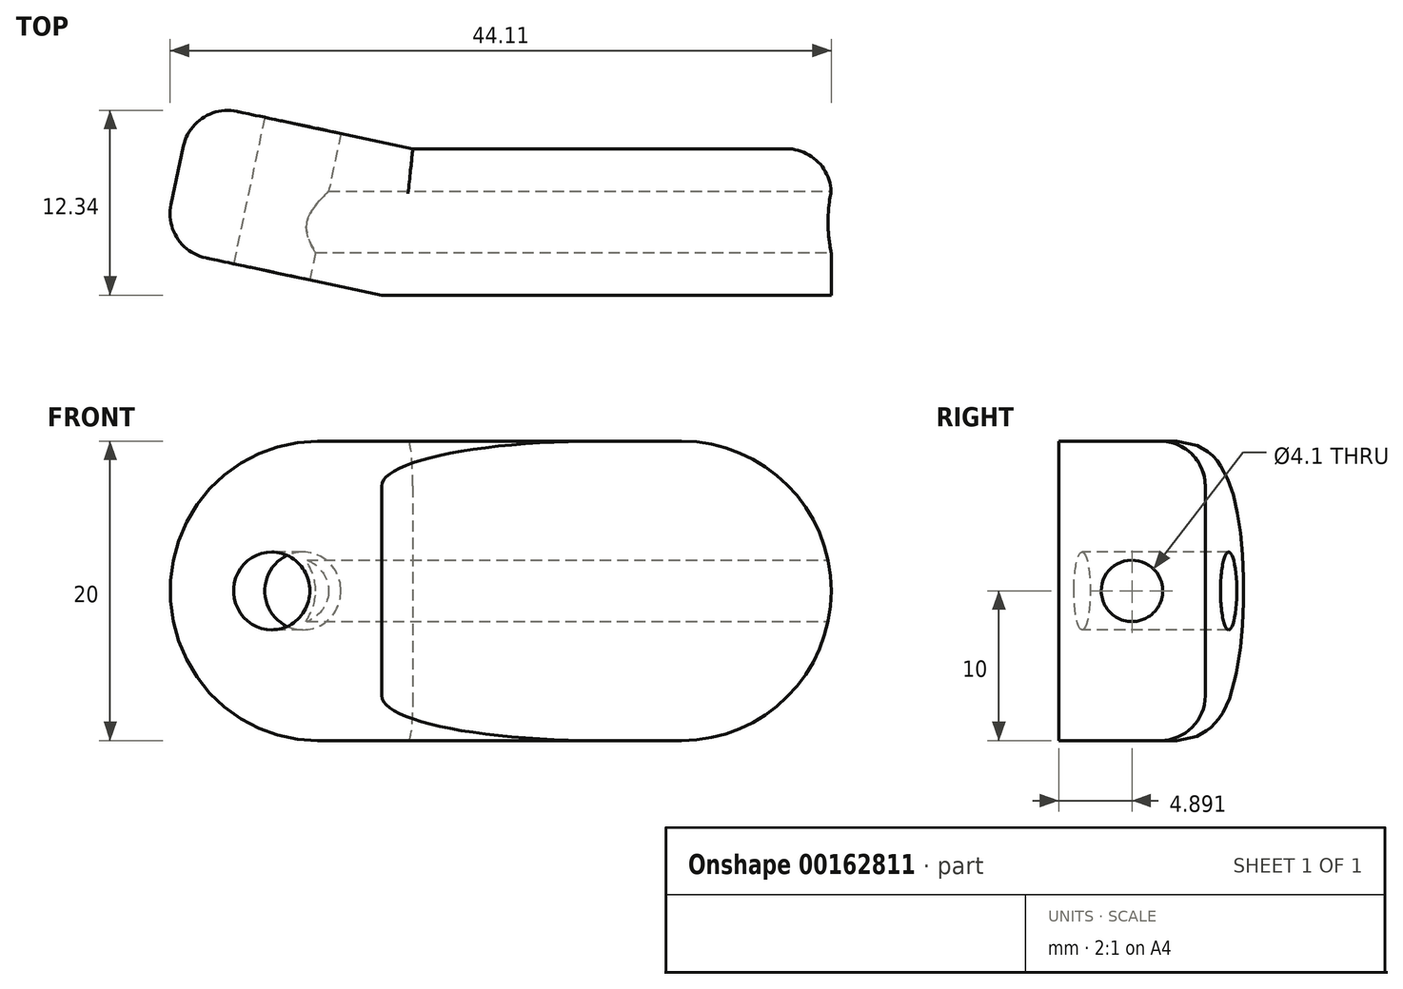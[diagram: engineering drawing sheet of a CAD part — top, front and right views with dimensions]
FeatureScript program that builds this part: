
annotation { "Feature Type Name" : "Feature", "Feature Type Description" : "" }
export const myFeature = defineFeature(function(context is Context, id is Id, definition is map)
    precondition{}
    {
        {
            var Q0;
            Q0=qCreatedBy(makeId("Top.planeOp"),FACE);
            var sketch = newSketch(context, id + "F0", { "sketchPlane" : qUnion([Q0])});
            skLineSegment(sketch, "E0", {"start": v(0, 0) * mm, "end": v(30, 0) * mm});
            skLineSegment(sketch, "E1", {"start": v(30, 0) * mm, "end": v(0, 0) * mm});
            skLineSegment(sketch, "E2", {"start": v(0, 0) * mm, "end": v(-14.67, 3.12) * mm});
            skLineSegment(sketch, "E3", {"start": v(-14.67, 3.12) * mm, "end": v(-12.6, 12.9) * mm});
            skLineSegment(sketch, "E4", {"start": v(2.08, 9.78) * mm, "end": v(-12.6, 12.9) * mm});
            skLineSegment(sketch, "E5", {"start": v(30, 0) * mm, "end": v(30, 9.78) * mm});
            skLineSegment(sketch, "E6", {"start": v(30, 9.78) * mm, "end": v(2.08, 9.78) * mm});
            skSolve(sketch);
        }
        {
            var Q0;
            Q0 = qSketchRegion(id + "F0", true);
            extrude(context, id + "F1", {"entities" : qUnion([Q0]), "depth" : 20 * mm});
        }
        {
            var Q0;
            Q0=makeQuery(id+"F1.opExtrude","SWEPT_FACE",FACE,{"disambiguationData":[OSD([sQuery(id+"F0.wireOp",EDGE,"E2")])]});
            var sketch = newSketch(context, id + "F2", { "sketchPlane" : qUnion([Q0])});
            skCircle(sketch, "E7", {"center": v(-7.5, 10) * mm, "radius": 2.6 * mm});
            skPoint(sketch, "E7.centerSnap0", {"position": v(0, 10) * mm});
            skPoint(sketch, "E7.centerSnap1", {"position": v(-7.5, 0) * mm});
            skSolve(sketch);
        }
        {
            var Q0;
            Q0 = qSketchRegion(id + "F2", true);
            extrude(context, id + "F3", {"entities" : qUnion([Q0]), "operationType" : NewBodyOperationType.REMOVE, "endBound" : BoundingType.THROUGH_ALL, "oppositeDirection" : true, "depth" : 25 * mm});
        }
        {
            var Q0;
            Q0=makeQuery(id+"F1.opExtrude","SWEPT_FACE",FACE,{"disambiguationData":[OSD([sQuery(id+"F0.wireOp",EDGE,"E5")])]});
            var sketch = newSketch(context, id + "F4", { "sketchPlane" : qUnion([Q0])});
            skCircle(sketch, "E8", {"center": v(4.9, 10) * mm, "radius": 2.05 * mm});
            skPoint(sketch, "E8.centerSnap0", {"position": v(0, 10) * mm});
            skPoint(sketch, "E8.centerSnap1", {"position": v(4.9, 0) * mm});
            skSolve(sketch);
        }
        {
            var Q0;
            Q0 = qSketchRegion(id + "F4", true);
            var Q1;
            Q1=makeQuery(id+"F3.boolean.opBoolean","COPY",FACE,{"derivedFrom":makeQuery(id+"F3.opExtrude","SWEPT_FACE",FACE,{"disambiguationData":[OSD([sQuery(id+"F2.wireOp",EDGE,"E7")])]})});
            extrude(context, id + "F5", {"entities" : qUnion([Q0]), "operationType" : NewBodyOperationType.REMOVE, "endBound" : BoundingType.UP_TO_SURFACE, "oppositeDirection" : true, "endBoundEntityFace" : qUnion([Q1]), "depth" : 30 * mm});
        }
        {
            var Q0;
            Q0=makeQuery(id+"F1.opExtrude","CAP_FACE",FACE,{"disambiguationData":[OSD([sQuery(id+"F0.wireOp",EDGE,"E1"),sQuery(id+"F0.wireOp",EDGE,"E2"),sQuery(id+"F0.wireOp",EDGE,"E3"),sQuery(id+"F0.wireOp",EDGE,"E4"),sQuery(id+"F0.wireOp",EDGE,"E5"),sQuery(id+"F0.wireOp",EDGE,"E6")])],"isStart":false});
            var sketch = newSketch(context, id + "F6", { "sketchPlane" : qUnion([Q0])});
            skLineSegment(sketch, "E9.bottom", {"start": v(30, 5.14) * mm, "end": v(10, 5.14) * mm});
            skLineSegment(sketch, "E9.top", {"start": v(30, 4.64) * mm, "end": v(10, 4.64) * mm});
            skLineSegment(sketch, "E9.left", {"start": v(30, 5.14) * mm, "end": v(30, 4.64) * mm});
            skLineSegment(sketch, "E9.right", {"start": v(10, 5.14) * mm, "end": v(10, 4.64) * mm});
            skPoint(sketch, "E10", {"position": v(30, 4.9) * mm});
            skSolve(sketch);
        }
        {
            var Q0;
            Q0=makeQuery(id+"F1.opExtrude","CAP_EDGE",EDGE,{"disambiguationData":[OSD([sQuery(id+"F0.wireOp",EDGE,"E3")])],"isStart":false});
            var Q1;
            Q1=makeQuery(id+"F1.opExtrude","CAP_EDGE",EDGE,{"disambiguationData":[OSD([sQuery(id+"F0.wireOp",EDGE,"E3")])],"isStart":true});
            var Q2;
            Q2=makeQuery(id+"F1.opExtrude","CAP_EDGE",EDGE,{"disambiguationData":[OSD([sQuery(id+"F0.wireOp",EDGE,"E5")])],"isStart":false});
            var Q3;
            Q3=makeQuery(id+"F1.opExtrude","CAP_EDGE",EDGE,{"disambiguationData":[OSD([sQuery(id+"F0.wireOp",EDGE,"E5")])],"isStart":true});
            fillet(context, id + "F7", {"entities" : qUnion([Q0, Q1, Q2, Q3]), "radius" : 10 * mm, "tangentPropagation" : true, "allowEdgeOverflow" : false});
        }
        {
            var Q0;
            Q0=makeQuery(id+"F1.opExtrude","SWEPT_EDGE",EDGE,{"disambiguationData":[OSD([sQuery(id+"F0.wireOp",EDGE,"E3"),sQuery(id+"F0.wireOp",EDGE,"E4")])]});
            var Q1;
            Q1=makeQuery(id+"F1.opExtrude","CAP_EDGE",EDGE,{"disambiguationData":[OSD([sQuery(id+"F0.wireOp",EDGE,"E2")])],"isStart":true});
            var Q2;
            Q2=makeQuery(id+"F1.opExtrude","CAP_EDGE",EDGE,{"disambiguationData":[OSD([sQuery(id+"F0.wireOp",EDGE,"E4")])],"isStart":true});
            var Q3;
            Q3=makeQuery(id+"F1.opExtrude","CAP_EDGE",EDGE,{"disambiguationData":[OSD([sQuery(id+"F0.wireOp",EDGE,"E6")])],"isStart":true});
            var Q4;
            Q4=makeQuery(id+"F1.opExtrude","CAP_EDGE",EDGE,{"disambiguationData":[OSD([sQuery(id+"F0.wireOp",EDGE,"E1")])],"isStart":true});
            var Q5;
            Q5=makeQuery(id+"F1.opExtrude","CAP_EDGE",EDGE,{"disambiguationData":[OSD([sQuery(id+"F0.wireOp",EDGE,"E2")])],"isStart":false});
            var Q6;
            Q6=makeQuery(id+"F1.opExtrude","CAP_EDGE",EDGE,{"disambiguationData":[OSD([sQuery(id+"F0.wireOp",EDGE,"E4")])],"isStart":false});
            var Q7;
            Q7=makeQuery(id+"F1.opExtrude","CAP_EDGE",EDGE,{"disambiguationData":[OSD([sQuery(id+"F0.wireOp",EDGE,"E6")])],"isStart":false});
            var Q8;
            Q8=makeQuery(id+"F1.opExtrude","CAP_EDGE",EDGE,{"disambiguationData":[OSD([sQuery(id+"F0.wireOp",EDGE,"E1")])],"isStart":false});
            fillet(context, id + "F8", {"entities" : qUnion([Q0, Q1, Q2, Q3, Q4, Q5, Q6, Q7, Q8]), "radius" : 3 * mm, "tangentPropagation" : true, "allowEdgeOverflow" : false});
        }
    });
